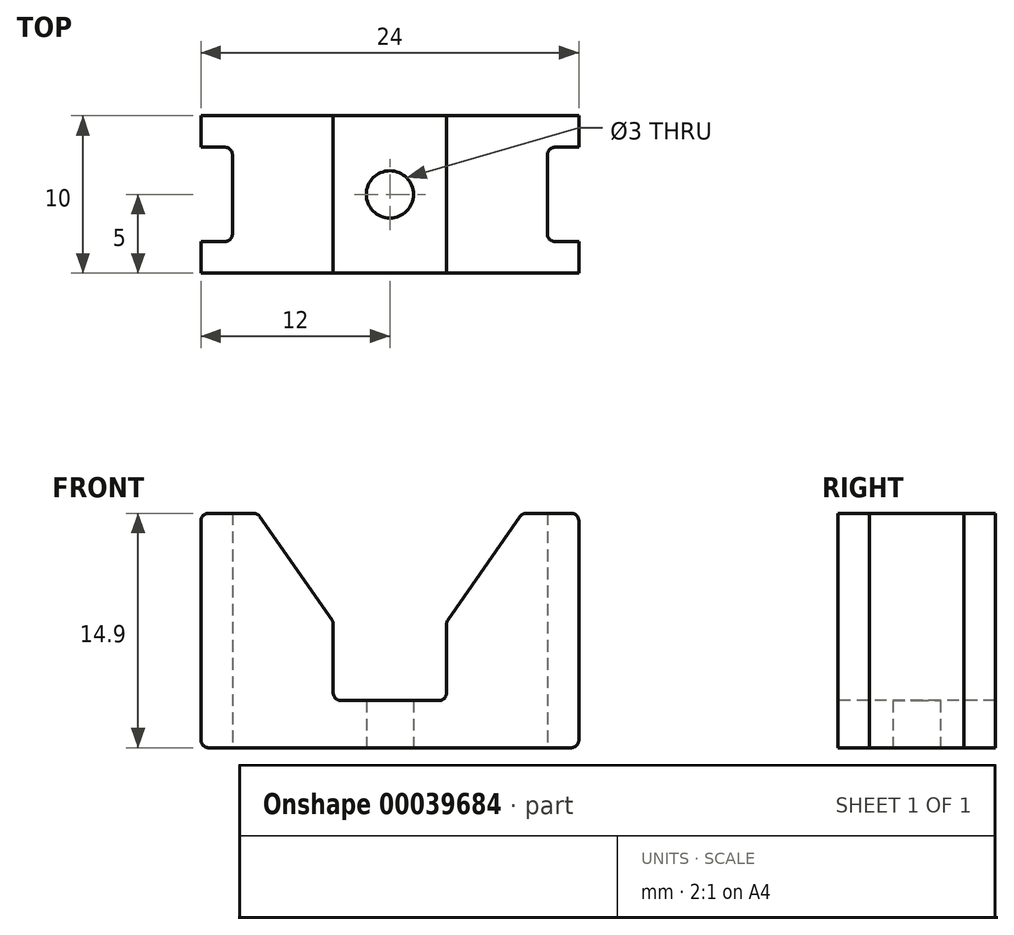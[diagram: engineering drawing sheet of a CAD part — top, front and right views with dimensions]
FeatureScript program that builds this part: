
annotation { "Feature Type Name" : "Feature", "Feature Type Description" : "" }
export const myFeature = defineFeature(function(context is Context, id is Id, definition is map)
    precondition{}
    {
        {
            var Q0;
            Q0=qCreatedBy(makeId("Front.planeOp"),FACE);
            var sketch = newSketch(context, id + "F0", { "sketchPlane" : qUnion([Q0])});
            skLineSegment(sketch, "E0", {"start": v(0, 0) * mm, "end": v(3.6, 0) * mm});
            skLineSegment(sketch, "E1", {"start": v(3.6, 0) * mm, "end": v(3.6, 5) * mm});
            skLineSegment(sketch, "E2", {"start": v(3.6, 5) * mm, "end": v(8.41, 11.9) * mm});
            skLineSegment(sketch, "E3", {"start": v(8.41, 11.9) * mm, "end": v(12, 11.9) * mm});
            skLineSegment(sketch, "E4", {"start": v(12, 11.9) * mm, "end": v(12, -3) * mm});
            skLineSegment(sketch, "E5", {"start": v(12, -3) * mm, "end": v(0, -3) * mm});
            skLineSegment(sketch, "E6", {"start": v(0, -3) * mm, "end": v(0, 0) * mm});
            skLineSegment(sketch, "E7.bottom", {"start": v(0, 0) * mm, "end": v(3.6, 0) * mm, "construction": true});
            skLineSegment(sketch, "E7.top", {"start": v(0, 5) * mm, "end": v(3.6, 5) * mm, "construction": true});
            skLineSegment(sketch, "E7.left", {"start": v(0, 0) * mm, "end": v(0, 5) * mm, "construction": true});
            skLineSegment(sketch, "E7.right", {"start": v(3.6, 0) * mm, "end": v(3.6, 5) * mm, "construction": true});
            skCircle(sketch, "E8", {"center": v(0, 11.9) * mm, "radius": 6.9 * mm, "construction": true});
            skSolve(sketch);
        }
        {
            var Q0;
            Q0=makeQuery(id+"F0.imprint","IMPRINT",FACE,{"disambiguationData":[TD([[makeQuery(id+"F0.imprint","IMPRINT",EDGE,{"derivedFrom":sQuery(id+"F0.wireOp",EDGE,"E0")}),-1.0]])]});
            extrude(context, id + "F1", {"entities" : qUnion([Q0]), "oppositeDirection" : true, "depth" : 10 * mm});
        }
        {
            var Q0;
            Q0=makeQuery(id+"F1.opExtrude","SWEPT_FACE",FACE,{"disambiguationData":[OSD([sQuery(id+"F0.wireOp",EDGE,"E4")])]});
            var sketch = newSketch(context, id + "F2", { "sketchPlane" : qUnion([Q0])});
            skLineSegment(sketch, "E9.bottom", {"start": v(8, 11.9) * mm, "end": v(2, 11.9) * mm});
            skLineSegment(sketch, "E9.top", {"start": v(8, -3) * mm, "end": v(2, -3) * mm});
            skLineSegment(sketch, "E9.left", {"start": v(8, 11.9) * mm, "end": v(8, -3) * mm});
            skLineSegment(sketch, "E9.right", {"start": v(2, 11.9) * mm, "end": v(2, -3) * mm});
            skSolve(sketch);
        }
        {
            var Q0;
            Q0=makeQuery(id+"F2.imprint","IMPRINT",FACE,{"disambiguationData":[TD([[makeQuery(id+"F2.imprint","IMPRINT",EDGE,{"derivedFrom":sQuery(id+"F2.wireOp",EDGE,"E9.bottom")}),1.0]])]});
            extrude(context, id + "F3", {"entities" : qUnion([Q0]), "operationType" : NewBodyOperationType.REMOVE, "oppositeDirection" : true, "depth" : 2 * mm});
        }
        {
            var Q0;
            Q0=makeQuery(id+"F1.opExtrude","SWEPT_BODY",BODY,{"disambiguationData":[OSD([sQuery(id+"F0.wireOp",EDGE,"E0"),sQuery(id+"F0.wireOp",EDGE,"E1"),sQuery(id+"F0.wireOp",EDGE,"E2"),sQuery(id+"F0.wireOp",EDGE,"E3"),sQuery(id+"F0.wireOp",EDGE,"E4"),sQuery(id+"F0.wireOp",EDGE,"E5"),sQuery(id+"F0.wireOp",EDGE,"E6")])]});
            var Q1;
            Q1=qCreatedBy(makeId("Right.planeOp"),FACE);
            mirror(context, id + "F4", {"operationType" : NewBodyOperationType.ADD, "entities" : qUnion([Q0]), "mirrorPlane" : qUnion([Q1])});
        }
        {
            var Q0;
            Q0=makeQuery(id+"F4.opPattern","COPY",EDGE,{"derivedFrom":makeQuery(id+"F1.opExtrude","SWEPT_EDGE",EDGE,{"disambiguationData":[OSD([sQuery(id+"F0.wireOp",EDGE,"E2"),sQuery(id+"F0.wireOp",EDGE,"E3")])]}),"instanceName":"1"});
            var Q1;
            Q1=makeQuery(id+"F4.opPattern","COPY",EDGE,{"derivedFrom":makeQuery(id+"F1.opExtrude","SWEPT_EDGE",EDGE,{"disambiguationData":[OSD([sQuery(id+"F0.wireOp",EDGE,"E3"),sQuery(id+"F0.wireOp",EDGE,"E4")])]}),"instanceName":"1"});
            var Q2;
            Q2=makeQuery(id+"F4.opPattern","COPY",EDGE,{"derivedFrom":makeQuery(id+"F1.opExtrude","SWEPT_EDGE",EDGE,{"disambiguationData":[OSD([sQuery(id+"F0.wireOp",EDGE,"E1"),sQuery(id+"F0.wireOp",EDGE,"E2")])]}),"instanceName":"1"});
            var Q3;
            Q3=makeQuery(id+"F4.opPattern","COPY",EDGE,{"derivedFrom":makeQuery(id+"F1.opExtrude","SWEPT_EDGE",EDGE,{"disambiguationData":[OSD([sQuery(id+"F0.wireOp",EDGE,"E0"),sQuery(id+"F0.wireOp",EDGE,"E1")])]}),"instanceName":"1"});
            var Q4;
            Q4=makeQuery(id+"F1.opExtrude","SWEPT_EDGE",EDGE,{"disambiguationData":[OSD([sQuery(id+"F0.wireOp",EDGE,"E0"),sQuery(id+"F0.wireOp",EDGE,"E1")])]});
            var Q5;
            Q5=makeQuery(id+"F1.opExtrude","SWEPT_EDGE",EDGE,{"disambiguationData":[OSD([sQuery(id+"F0.wireOp",EDGE,"E1"),sQuery(id+"F0.wireOp",EDGE,"E2")])]});
            var Q6;
            Q6=makeQuery(id+"F1.opExtrude","SWEPT_EDGE",EDGE,{"disambiguationData":[OSD([sQuery(id+"F0.wireOp",EDGE,"E2"),sQuery(id+"F0.wireOp",EDGE,"E3")])]});
            var Q7;
            Q7=makeQuery(id+"F1.opExtrude","SWEPT_EDGE",EDGE,{"disambiguationData":[OSD([sQuery(id+"F0.wireOp",EDGE,"E3"),sQuery(id+"F0.wireOp",EDGE,"E4")])]});
            var Q8;
            Q8=makeQuery(id+"F1.opExtrude","SWEPT_EDGE",EDGE,{"disambiguationData":[OSD([sQuery(id+"F0.wireOp",EDGE,"E4"),sQuery(id+"F0.wireOp",EDGE,"E5")])]});
            var Q9;
            Q9=makeQuery(id+"F4.opPattern","COPY",EDGE,{"derivedFrom":makeQuery(id+"F1.opExtrude","SWEPT_EDGE",EDGE,{"disambiguationData":[OSD([sQuery(id+"F0.wireOp",EDGE,"E4"),sQuery(id+"F0.wireOp",EDGE,"E5")])]}),"instanceName":"1"});
            var Q10;
            Q10=makeQuery(id+"F3.boolean.opBoolean","COPY",EDGE,{"derivedFrom":makeQuery(id+"F3.opExtrude","CAP_EDGE",EDGE,{"disambiguationData":[OSD([sQuery(id+"F2.wireOp",EDGE,"E9.left")])],"isStart":false})});
            var Q11;
            Q11=makeQuery(id+"F3.boolean.opBoolean","COPY",EDGE,{"derivedFrom":makeQuery(id+"F3.opExtrude","CAP_EDGE",EDGE,{"disambiguationData":[OSD([sQuery(id+"F2.wireOp",EDGE,"E9.right")])],"isStart":false})});
            var Q12;
            Q12=makeQuery(id+"F4.opPattern","COPY",EDGE,{"derivedFrom":makeQuery(id+"F3.boolean.opBoolean","COPY",EDGE,{"derivedFrom":makeQuery(id+"F3.opExtrude","CAP_EDGE",EDGE,{"disambiguationData":[OSD([sQuery(id+"F2.wireOp",EDGE,"E9.right")])],"isStart":false})}),"instanceName":"1"});
            var Q13;
            Q13=makeQuery(id+"F4.opPattern","COPY",EDGE,{"derivedFrom":makeQuery(id+"F3.boolean.opBoolean","COPY",EDGE,{"derivedFrom":makeQuery(id+"F3.opExtrude","CAP_EDGE",EDGE,{"disambiguationData":[OSD([sQuery(id+"F2.wireOp",EDGE,"E9.left")])],"isStart":false})}),"instanceName":"1"});
            fillet(context, id + "F5", {"entities" : qUnion([Q0, Q1, Q2, Q3, Q4, Q5, Q6, Q7, Q8, Q9, Q10, Q11, Q12, Q13]), "radius" : 0.5 * mm, "tangentPropagation" : true, "allowEdgeOverflow" : false});
        }
        {
            var Q0;
            {var subQ0=makeQuery(id+"F1.opExtrude","SWEPT_FACE",FACE,{"disambiguationData":[OSD([sQuery(id+"F0.wireOp",EDGE,"E5")])]});Q0=makeQuery(id+"F4.boolean.opBoolean","MERGE",FACE,{"derivedFrom":[subQ0,makeQuery(id+"F4.opPattern","COPY",FACE,{"derivedFrom":subQ0,"instanceName":"1"})]});}
            var sketch = newSketch(context, id + "F6", { "sketchPlane" : qUnion([Q0])});
            skPoint(sketch, "E10", {"position": v(0, -5) * mm});
            skSolve(sketch);
        }
        {
            var Q0;
            Q0=sQuery(id+"F6.wireOp",VERTEX,"E10");
            var Q1;
            Q1=makeQuery(id+"F1.opExtrude","SWEPT_BODY",BODY,{"disambiguationData":[OSD([sQuery(id+"F0.wireOp",EDGE,"E0"),sQuery(id+"F0.wireOp",EDGE,"E1"),sQuery(id+"F0.wireOp",EDGE,"E2"),sQuery(id+"F0.wireOp",EDGE,"E3"),sQuery(id+"F0.wireOp",EDGE,"E4"),sQuery(id+"F0.wireOp",EDGE,"E5"),sQuery(id+"F0.wireOp",EDGE,"E6")])]});
            hole(context, id + "F7", {"style" : HoleStyle.SIMPLE, "holeDiameter" : 3 * mm, "endStyle" : HoleEndStyle.THROUGH, "locations" : qUnion([Q0]), "scope" : qUnion([Q1])});
        }
    });
